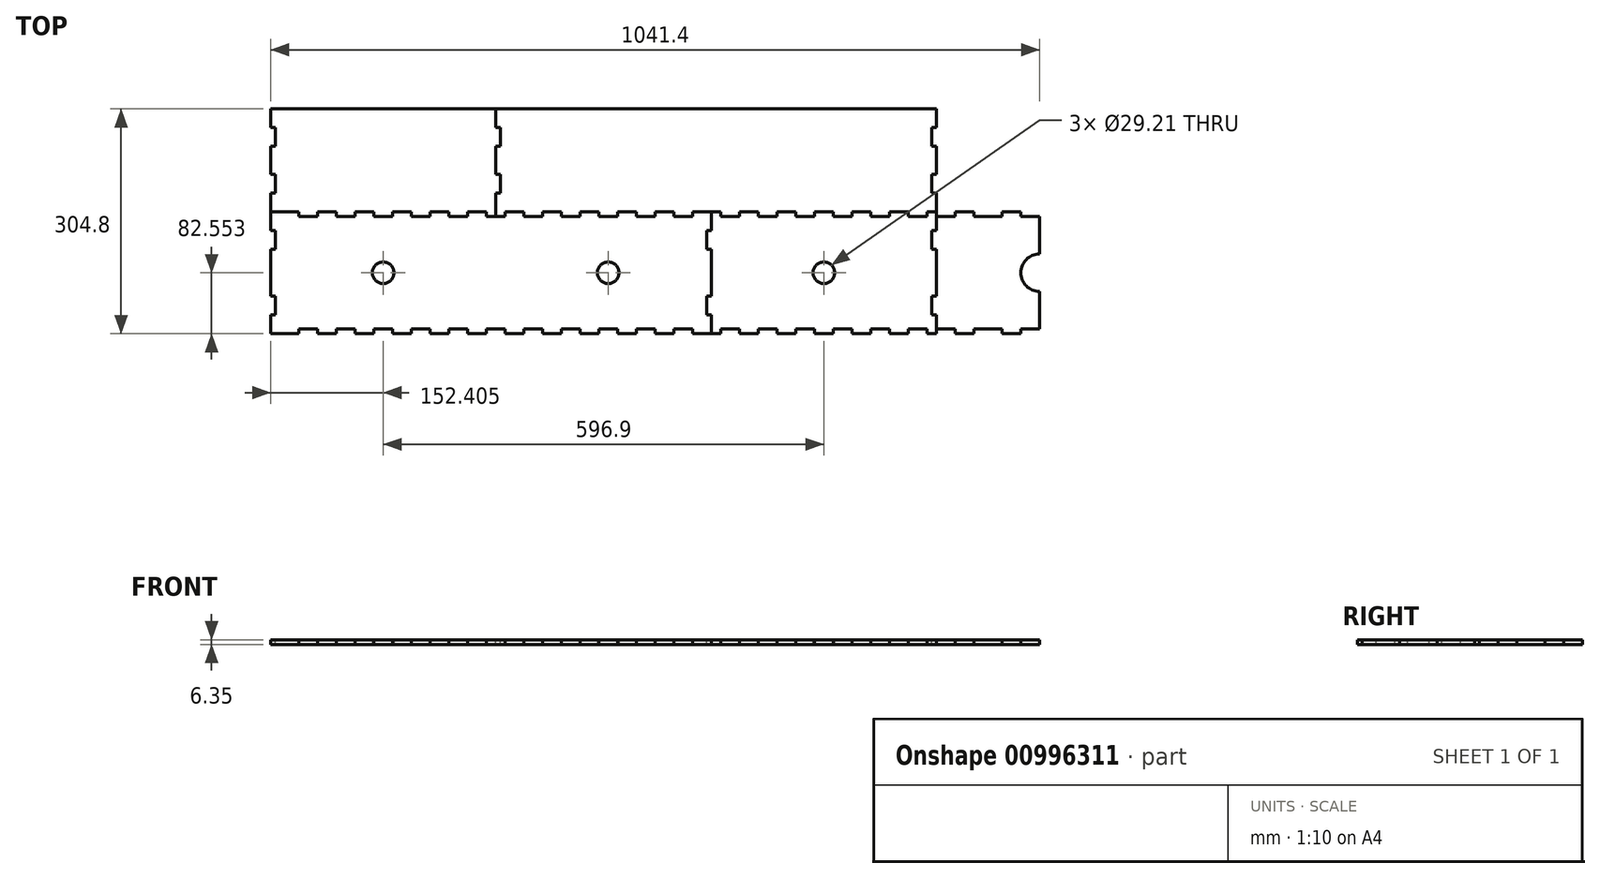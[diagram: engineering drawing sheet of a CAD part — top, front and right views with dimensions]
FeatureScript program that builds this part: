
annotation { "Feature Type Name" : "Feature", "Feature Type Description" : "" }
export const myFeature = defineFeature(function(context is Context, id is Id, definition is map)
    precondition{}
    {
        {
            var Q0;
            Q0=qCreatedBy(makeId("Top.planeOp"),FACE);
            var sketch = newSketch(context, id + "F0", { "sketchPlane" : qUnion([Q0])});
            skLineSegment(sketch, "E0.bottom", {"start": v(-304.97, 96.31) * mm, "end": v(291.93, 96.31) * mm});
            skLineSegment(sketch, "E0.top", {"start": v(-304.97, -68.79) * mm, "end": v(291.93, -68.79) * mm});
            skLineSegment(sketch, "E0.left", {"start": v(-304.97, 96.31) * mm, "end": v(-304.97, -68.79) * mm});
            skLineSegment(sketch, "E0.right", {"start": v(291.93, 96.31) * mm, "end": v(291.93, -68.79) * mm});
            skLineSegment(sketch, "E1.bottom", {"start": v(-266.87, 96.31) * mm, "end": v(-241.47, 96.31) * mm});
            skLineSegment(sketch, "E1.top", {"start": v(-266.87, 89.96) * mm, "end": v(-241.47, 89.96) * mm});
            skLineSegment(sketch, "E1.left", {"start": v(-266.87, 96.31) * mm, "end": v(-266.87, 89.96) * mm});
            skLineSegment(sketch, "E1.right", {"start": v(-241.47, 96.31) * mm, "end": v(-241.47, 89.96) * mm});
            skLineSegment(sketch, "E2.1.0.0", {"start": v(-216.07, 89.96) * mm, "end": v(-190.67, 89.96) * mm});
            skLineSegment(sketch, "E2.1.0.1", {"start": v(-216.07, 96.31) * mm, "end": v(-216.07, 89.96) * mm});
            skLineSegment(sketch, "E2.1.0.2", {"start": v(-216.07, 96.31) * mm, "end": v(-190.67, 96.31) * mm});
            skLineSegment(sketch, "E2.1.0.3", {"start": v(-190.67, 96.31) * mm, "end": v(-190.67, 89.96) * mm});
            skLineSegment(sketch, "E2.2.0.0", {"start": v(-165.27, 89.96) * mm, "end": v(-139.87, 89.96) * mm});
            skLineSegment(sketch, "E2.2.0.1", {"start": v(-165.27, 96.31) * mm, "end": v(-165.27, 89.96) * mm});
            skLineSegment(sketch, "E2.2.0.2", {"start": v(-165.27, 96.31) * mm, "end": v(-139.87, 96.31) * mm});
            skLineSegment(sketch, "E2.2.0.3", {"start": v(-139.87, 96.31) * mm, "end": v(-139.87, 89.96) * mm});
            skLineSegment(sketch, "E2.3.0.0", {"start": v(-114.47, 89.96) * mm, "end": v(-89.07, 89.96) * mm});
            skLineSegment(sketch, "E2.3.0.1", {"start": v(-114.47, 96.31) * mm, "end": v(-114.47, 89.96) * mm});
            skLineSegment(sketch, "E2.3.0.2", {"start": v(-114.47, 96.31) * mm, "end": v(-89.07, 96.31) * mm});
            skLineSegment(sketch, "E2.3.0.3", {"start": v(-89.07, 96.31) * mm, "end": v(-89.07, 89.96) * mm});
            skLineSegment(sketch, "E2.4.0.0", {"start": v(-63.67, 89.96) * mm, "end": v(-38.27, 89.96) * mm});
            skLineSegment(sketch, "E2.4.0.1", {"start": v(-63.67, 96.31) * mm, "end": v(-63.67, 89.96) * mm});
            skLineSegment(sketch, "E2.4.0.2", {"start": v(-63.67, 96.31) * mm, "end": v(-38.27, 96.31) * mm});
            skLineSegment(sketch, "E2.4.0.3", {"start": v(-38.27, 96.31) * mm, "end": v(-38.27, 89.96) * mm});
            skLineSegment(sketch, "E2.5.0.0", {"start": v(-12.87, 89.96) * mm, "end": v(12.53, 89.96) * mm});
            skLineSegment(sketch, "E2.5.0.1", {"start": v(-12.87, 96.31) * mm, "end": v(-12.87, 89.96) * mm});
            skLineSegment(sketch, "E2.5.0.2", {"start": v(-12.87, 96.31) * mm, "end": v(12.53, 96.31) * mm});
            skLineSegment(sketch, "E2.5.0.3", {"start": v(12.53, 96.31) * mm, "end": v(12.53, 89.96) * mm});
            skLineSegment(sketch, "E2.6.0.0", {"start": v(37.93, 89.96) * mm, "end": v(63.33, 89.96) * mm});
            skLineSegment(sketch, "E2.6.0.1", {"start": v(37.93, 96.31) * mm, "end": v(37.93, 89.96) * mm});
            skLineSegment(sketch, "E2.6.0.2", {"start": v(37.93, 96.31) * mm, "end": v(63.33, 96.31) * mm});
            skLineSegment(sketch, "E2.6.0.3", {"start": v(63.33, 96.31) * mm, "end": v(63.33, 89.96) * mm});
            skLineSegment(sketch, "E2.7.0.0", {"start": v(88.73, 89.96) * mm, "end": v(114.13, 89.96) * mm});
            skLineSegment(sketch, "E2.7.0.1", {"start": v(88.73, 96.31) * mm, "end": v(88.73, 89.96) * mm});
            skLineSegment(sketch, "E2.7.0.2", {"start": v(88.73, 96.31) * mm, "end": v(114.13, 96.31) * mm});
            skLineSegment(sketch, "E2.7.0.3", {"start": v(114.13, 96.31) * mm, "end": v(114.13, 89.96) * mm});
            skLineSegment(sketch, "E2.8.0.0", {"start": v(139.53, 89.96) * mm, "end": v(164.93, 89.96) * mm});
            skLineSegment(sketch, "E2.8.0.1", {"start": v(139.53, 96.31) * mm, "end": v(139.53, 89.96) * mm});
            skLineSegment(sketch, "E2.8.0.2", {"start": v(139.53, 96.31) * mm, "end": v(164.93, 96.31) * mm});
            skLineSegment(sketch, "E2.8.0.3", {"start": v(164.93, 96.31) * mm, "end": v(164.93, 89.96) * mm});
            skLineSegment(sketch, "E2.9.0.0", {"start": v(190.33, 89.96) * mm, "end": v(215.73, 89.96) * mm});
            skLineSegment(sketch, "E2.9.0.1", {"start": v(190.33, 96.31) * mm, "end": v(190.33, 89.96) * mm});
            skLineSegment(sketch, "E2.9.0.2", {"start": v(190.33, 96.31) * mm, "end": v(215.73, 96.31) * mm});
            skLineSegment(sketch, "E2.9.0.3", {"start": v(215.73, 96.31) * mm, "end": v(215.73, 89.96) * mm});
            skLineSegment(sketch, "E2.10.0.0", {"start": v(241.13, 89.96) * mm, "end": v(266.53, 89.96) * mm});
            skLineSegment(sketch, "E2.10.0.1", {"start": v(241.13, 96.31) * mm, "end": v(241.13, 89.96) * mm});
            skLineSegment(sketch, "E2.10.0.2", {"start": v(241.13, 96.31) * mm, "end": v(266.53, 96.31) * mm});
            skLineSegment(sketch, "E2.10.0.3", {"start": v(266.53, 96.31) * mm, "end": v(266.53, 89.96) * mm});
            skLineSegment(sketch, "E2.direction1", {"start": v(-266.87, 89.96) * mm, "end": v(-216.07, 89.96) * mm, "construction": true});
            skLineSegment(sketch, "E3.bottom", {"start": v(-266.87, -62.44) * mm, "end": v(-241.47, -62.44) * mm});
            skLineSegment(sketch, "E3.top", {"start": v(-266.87, -68.79) * mm, "end": v(-241.47, -68.79) * mm});
            skLineSegment(sketch, "E3.left", {"start": v(-266.87, -62.44) * mm, "end": v(-266.87, -68.79) * mm});
            skLineSegment(sketch, "E3.right", {"start": v(-241.47, -62.44) * mm, "end": v(-241.47, -68.79) * mm});
            skLineSegment(sketch, "E4.1.0.0", {"start": v(-216.07, -68.79) * mm, "end": v(-190.67, -68.79) * mm});
            skLineSegment(sketch, "E4.1.0.1", {"start": v(-216.07, -62.44) * mm, "end": v(-216.07, -68.79) * mm});
            skLineSegment(sketch, "E4.1.0.2", {"start": v(-216.07, -62.44) * mm, "end": v(-190.67, -62.44) * mm});
            skLineSegment(sketch, "E4.1.0.3", {"start": v(-190.67, -62.44) * mm, "end": v(-190.67, -68.79) * mm});
            skLineSegment(sketch, "E4.2.0.0", {"start": v(-165.27, -68.79) * mm, "end": v(-139.87, -68.79) * mm});
            skLineSegment(sketch, "E4.2.0.1", {"start": v(-165.27, -62.44) * mm, "end": v(-165.27, -68.79) * mm});
            skLineSegment(sketch, "E4.2.0.2", {"start": v(-165.27, -62.44) * mm, "end": v(-139.87, -62.44) * mm});
            skLineSegment(sketch, "E4.2.0.3", {"start": v(-139.87, -62.44) * mm, "end": v(-139.87, -68.79) * mm});
            skLineSegment(sketch, "E4.3.0.0", {"start": v(-114.47, -68.79) * mm, "end": v(-89.07, -68.79) * mm});
            skLineSegment(sketch, "E4.3.0.1", {"start": v(-114.47, -62.44) * mm, "end": v(-114.47, -68.79) * mm});
            skLineSegment(sketch, "E4.3.0.2", {"start": v(-114.47, -62.44) * mm, "end": v(-89.07, -62.44) * mm});
            skLineSegment(sketch, "E4.3.0.3", {"start": v(-89.07, -62.44) * mm, "end": v(-89.07, -68.79) * mm});
            skLineSegment(sketch, "E4.4.0.0", {"start": v(-63.67, -68.79) * mm, "end": v(-38.27, -68.79) * mm});
            skLineSegment(sketch, "E4.4.0.1", {"start": v(-63.67, -62.44) * mm, "end": v(-63.67, -68.79) * mm});
            skLineSegment(sketch, "E4.4.0.2", {"start": v(-63.67, -62.44) * mm, "end": v(-38.27, -62.44) * mm});
            skLineSegment(sketch, "E4.4.0.3", {"start": v(-38.27, -62.44) * mm, "end": v(-38.27, -68.79) * mm});
            skLineSegment(sketch, "E4.5.0.0", {"start": v(-12.87, -68.79) * mm, "end": v(12.53, -68.79) * mm});
            skLineSegment(sketch, "E4.5.0.1", {"start": v(-12.87, -62.44) * mm, "end": v(-12.87, -68.79) * mm});
            skLineSegment(sketch, "E4.5.0.2", {"start": v(-12.87, -62.44) * mm, "end": v(12.53, -62.44) * mm});
            skLineSegment(sketch, "E4.5.0.3", {"start": v(12.53, -62.44) * mm, "end": v(12.53, -68.79) * mm});
            skLineSegment(sketch, "E4.6.0.0", {"start": v(37.93, -68.79) * mm, "end": v(63.33, -68.79) * mm});
            skLineSegment(sketch, "E4.6.0.1", {"start": v(37.93, -62.44) * mm, "end": v(37.93, -68.79) * mm});
            skLineSegment(sketch, "E4.6.0.2", {"start": v(37.93, -62.44) * mm, "end": v(63.33, -62.44) * mm});
            skLineSegment(sketch, "E4.6.0.3", {"start": v(63.33, -62.44) * mm, "end": v(63.33, -68.79) * mm});
            skLineSegment(sketch, "E4.7.0.0", {"start": v(88.73, -68.79) * mm, "end": v(114.13, -68.79) * mm});
            skLineSegment(sketch, "E4.7.0.1", {"start": v(88.73, -62.44) * mm, "end": v(88.73, -68.79) * mm});
            skLineSegment(sketch, "E4.7.0.2", {"start": v(88.73, -62.44) * mm, "end": v(114.13, -62.44) * mm});
            skLineSegment(sketch, "E4.7.0.3", {"start": v(114.13, -62.44) * mm, "end": v(114.13, -68.79) * mm});
            skLineSegment(sketch, "E4.8.0.0", {"start": v(139.53, -68.79) * mm, "end": v(164.93, -68.79) * mm});
            skLineSegment(sketch, "E4.8.0.1", {"start": v(139.53, -62.44) * mm, "end": v(139.53, -68.79) * mm});
            skLineSegment(sketch, "E4.8.0.2", {"start": v(139.53, -62.44) * mm, "end": v(164.93, -62.44) * mm});
            skLineSegment(sketch, "E4.8.0.3", {"start": v(164.93, -62.44) * mm, "end": v(164.93, -68.79) * mm});
            skLineSegment(sketch, "E4.9.0.0", {"start": v(190.33, -68.79) * mm, "end": v(215.73, -68.79) * mm});
            skLineSegment(sketch, "E4.9.0.1", {"start": v(190.33, -62.44) * mm, "end": v(190.33, -68.79) * mm});
            skLineSegment(sketch, "E4.9.0.2", {"start": v(190.33, -62.44) * mm, "end": v(215.73, -62.44) * mm});
            skLineSegment(sketch, "E4.9.0.3", {"start": v(215.73, -62.44) * mm, "end": v(215.73, -68.79) * mm});
            skLineSegment(sketch, "E4.10.0.0", {"start": v(241.13, -68.79) * mm, "end": v(266.53, -68.79) * mm});
            skLineSegment(sketch, "E4.10.0.1", {"start": v(241.13, -62.44) * mm, "end": v(241.13, -68.79) * mm});
            skLineSegment(sketch, "E4.10.0.2", {"start": v(241.13, -62.44) * mm, "end": v(266.53, -62.44) * mm});
            skLineSegment(sketch, "E4.10.0.3", {"start": v(266.53, -62.44) * mm, "end": v(266.53, -68.79) * mm});
            skLineSegment(sketch, "E4.direction1", {"start": v(-266.87, -68.79) * mm, "end": v(-216.07, -68.79) * mm, "construction": true});
            skLineSegment(sketch, "E5.bottom", {"start": v(-304.97, 70.91) * mm, "end": v(-298.62, 70.91) * mm});
            skLineSegment(sketch, "E5.top", {"start": v(-304.97, 45.51) * mm, "end": v(-298.62, 45.51) * mm});
            skLineSegment(sketch, "E5.left", {"start": v(-304.97, 70.91) * mm, "end": v(-304.97, 45.51) * mm});
            skLineSegment(sketch, "E5.right", {"start": v(-298.62, 70.91) * mm, "end": v(-298.62, 45.51) * mm});
            skLineSegment(sketch, "E6.bottom", {"start": v(-304.97, -17.99) * mm, "end": v(-298.62, -17.99) * mm});
            skLineSegment(sketch, "E6.top", {"start": v(-304.97, -43.39) * mm, "end": v(-298.62, -43.39) * mm});
            skLineSegment(sketch, "E6.left", {"start": v(-304.97, -17.99) * mm, "end": v(-304.97, -43.39) * mm});
            skLineSegment(sketch, "E6.right", {"start": v(-298.62, -17.99) * mm, "end": v(-298.62, -43.39) * mm});
            skLineSegment(sketch, "E7.bottom", {"start": v(285.58, 70.91) * mm, "end": v(291.93, 70.91) * mm});
            skLineSegment(sketch, "E7.top", {"start": v(285.58, 45.51) * mm, "end": v(291.93, 45.51) * mm});
            skLineSegment(sketch, "E7.left", {"start": v(285.58, 70.91) * mm, "end": v(285.58, 45.51) * mm});
            skLineSegment(sketch, "E7.right", {"start": v(291.93, 70.91) * mm, "end": v(291.93, 45.51) * mm, "construction": true});
            skLineSegment(sketch, "E8.bottom", {"start": v(285.58, -17.99) * mm, "end": v(291.93, -17.99) * mm});
            skLineSegment(sketch, "E8.top", {"start": v(285.58, -43.39) * mm, "end": v(291.93, -43.39) * mm});
            skLineSegment(sketch, "E8.left", {"start": v(285.58, -17.99) * mm, "end": v(285.58, -43.39) * mm});
            skLineSegment(sketch, "E8.right", {"start": v(291.93, -17.99) * mm, "end": v(291.93, -43.39) * mm});
            skCircle(sketch, "E9", {"center": v(-152.57, 13.76) * mm, "radius": 14.6 * mm});
            skCircle(sketch, "E10", {"center": v(152.23, 13.76) * mm, "radius": 14.6 * mm});
            skSolve(sketch);
        }
        {
            var Q0;
            Q0=makeQuery(id+"F0.imprint","IMPRINT",FACE,{"disambiguationData":[TD([[makeQuery(id+"F0.imprint","IMPRINT",EDGE,{"derivedFrom":sQuery(id+"F0.wireOp",EDGE,"E1.top")}),-1.0]])]});
            extrude(context, id + "F1", {"entities" : qUnion([Q0]), "depth" : 6.35 * mm, "offsetDistance" : 25.4 * mm});
        }
        {
            var Q0;
            Q0=makeQuery(id+"F1.opExtrude","CAP_FACE",FACE,{"disambiguationData":[OSD([sQuery(id+"F0.wireOp",EDGE,"E0.bottom"),sQuery(id+"F0.wireOp",EDGE,"E0.top"),sQuery(id+"F0.wireOp",EDGE,"E0.left"),sQuery(id+"F0.wireOp",EDGE,"E0.right"),sQuery(id+"F0.wireOp",EDGE,"E1.top"),sQuery(id+"F0.wireOp",EDGE,"E1.left"),sQuery(id+"F0.wireOp",EDGE,"E1.right"),sQuery(id+"F0.wireOp",EDGE,"E2.1.0.0"),sQuery(id+"F0.wireOp",EDGE,"E2.1.0.1"),sQuery(id+"F0.wireOp",EDGE,"E2.1.0.3"),sQuery(id+"F0.wireOp",EDGE,"E2.2.0.0"),sQuery(id+"F0.wireOp",EDGE,"E2.2.0.1"),sQuery(id+"F0.wireOp",EDGE,"E2.2.0.3"),sQuery(id+"F0.wireOp",EDGE,"E2.3.0.0"),sQuery(id+"F0.wireOp",EDGE,"E2.3.0.1"),sQuery(id+"F0.wireOp",EDGE,"E2.3.0.3"),sQuery(id+"F0.wireOp",EDGE,"E2.4.0.0"),sQuery(id+"F0.wireOp",EDGE,"E2.4.0.1"),sQuery(id+"F0.wireOp",EDGE,"E2.4.0.3"),sQuery(id+"F0.wireOp",EDGE,"E2.5.0.0"),sQuery(id+"F0.wireOp",EDGE,"E2.5.0.1"),sQuery(id+"F0.wireOp",EDGE,"E2.5.0.3"),sQuery(id+"F0.wireOp",EDGE,"E2.6.0.0"),sQuery(id+"F0.wireOp",EDGE,"E2.6.0.1"),sQuery(id+"F0.wireOp",EDGE,"E2.6.0.3"),sQuery(id+"F0.wireOp",EDGE,"E2.7.0.0"),sQuery(id+"F0.wireOp",EDGE,"E2.7.0.1"),sQuery(id+"F0.wireOp",EDGE,"E2.7.0.3"),sQuery(id+"F0.wireOp",EDGE,"E2.8.0.0"),sQuery(id+"F0.wireOp",EDGE,"E2.8.0.1"),sQuery(id+"F0.wireOp",EDGE,"E2.8.0.3"),sQuery(id+"F0.wireOp",EDGE,"E2.9.0.0"),sQuery(id+"F0.wireOp",EDGE,"E2.9.0.1"),sQuery(id+"F0.wireOp",EDGE,"E2.9.0.3"),sQuery(id+"F0.wireOp",EDGE,"E2.10.0.0"),sQuery(id+"F0.wireOp",EDGE,"E2.10.0.1"),sQuery(id+"F0.wireOp",EDGE,"E2.10.0.3"),sQuery(id+"F0.wireOp",EDGE,"E3.bottom"),sQuery(id+"F0.wireOp",EDGE,"E3.left"),sQuery(id+"F0.wireOp",EDGE,"E3.right"),sQuery(id+"F0.wireOp",EDGE,"E4.1.0.1"),sQuery(id+"F0.wireOp",EDGE,"E4.1.0.2"),sQuery(id+"F0.wireOp",EDGE,"E4.1.0.3"),sQuery(id+"F0.wireOp",EDGE,"E4.2.0.1"),sQuery(id+"F0.wireOp",EDGE,"E4.2.0.2"),sQuery(id+"F0.wireOp",EDGE,"E4.2.0.3"),sQuery(id+"F0.wireOp",EDGE,"E4.3.0.1"),sQuery(id+"F0.wireOp",EDGE,"E4.3.0.2"),sQuery(id+"F0.wireOp",EDGE,"E4.3.0.3"),sQuery(id+"F0.wireOp",EDGE,"E4.4.0.1"),sQuery(id+"F0.wireOp",EDGE,"E4.4.0.2"),sQuery(id+"F0.wireOp",EDGE,"E4.4.0.3"),sQuery(id+"F0.wireOp",EDGE,"E4.5.0.1"),sQuery(id+"F0.wireOp",EDGE,"E4.5.0.2"),sQuery(id+"F0.wireOp",EDGE,"E4.5.0.3"),sQuery(id+"F0.wireOp",EDGE,"E4.6.0.1"),sQuery(id+"F0.wireOp",EDGE,"E4.6.0.2"),sQuery(id+"F0.wireOp",EDGE,"E4.6.0.3"),sQuery(id+"F0.wireOp",EDGE,"E4.7.0.1"),sQuery(id+"F0.wireOp",EDGE,"E4.7.0.2"),sQuery(id+"F0.wireOp",EDGE,"E4.7.0.3"),sQuery(id+"F0.wireOp",EDGE,"E4.8.0.1"),sQuery(id+"F0.wireOp",EDGE,"E4.8.0.2"),sQuery(id+"F0.wireOp",EDGE,"E4.8.0.3"),sQuery(id+"F0.wireOp",EDGE,"E4.9.0.1"),sQuery(id+"F0.wireOp",EDGE,"E4.9.0.2"),sQuery(id+"F0.wireOp",EDGE,"E4.9.0.3"),sQuery(id+"F0.wireOp",EDGE,"E4.10.0.1"),sQuery(id+"F0.wireOp",EDGE,"E4.10.0.2"),sQuery(id+"F0.wireOp",EDGE,"E4.10.0.3"),sQuery(id+"F0.wireOp",EDGE,"E5.bottom"),sQuery(id+"F0.wireOp",EDGE,"E5.top"),sQuery(id+"F0.wireOp",EDGE,"E5.right"),sQuery(id+"F0.wireOp",EDGE,"E6.bottom"),sQuery(id+"F0.wireOp",EDGE,"E6.top"),sQuery(id+"F0.wireOp",EDGE,"E6.right"),sQuery(id+"F0.wireOp",EDGE,"E7.bottom"),sQuery(id+"F0.wireOp",EDGE,"E7.top"),sQuery(id+"F0.wireOp",EDGE,"E7.left"),sQuery(id+"F0.wireOp",EDGE,"E8.bottom"),sQuery(id+"F0.wireOp",EDGE,"E8.top"),sQuery(id+"F0.wireOp",EDGE,"E8.left"),sQuery(id+"F0.wireOp",EDGE,"E9"),sQuery(id+"F0.wireOp",EDGE,"E10")])],"isStart":false});
            var sketch = newSketch(context, id + "F2", { "sketchPlane" : qUnion([Q0])});
            skLineSegment(sketch, "E11.bottom", {"start": v(291.93, 96.31) * mm, "end": v(596.73, 96.31) * mm});
            skLineSegment(sketch, "E11.top", {"start": v(291.93, -68.79) * mm, "end": v(596.73, -68.79) * mm});
            skLineSegment(sketch, "E11.left", {"start": v(291.93, 96.31) * mm, "end": v(291.93, 70.91) * mm});
            skLineSegment(sketch, "E11.right", {"start": v(596.73, 96.31) * mm, "end": v(596.73, -68.79) * mm});
            skLineSegment(sketch, "E12.bottom", {"start": v(291.93, 70.91) * mm, "end": v(285.58, 70.91) * mm});
            skLineSegment(sketch, "E12.top", {"start": v(291.93, 45.51) * mm, "end": v(285.58, 45.51) * mm});
            skLineSegment(sketch, "E12.right", {"start": v(285.58, 70.91) * mm, "end": v(285.58, 45.51) * mm});
            skLineSegment(sketch, "E13.bottom", {"start": v(291.93, -17.99) * mm, "end": v(285.58, -17.99) * mm});
            skLineSegment(sketch, "E13.top", {"start": v(291.93, -43.39) * mm, "end": v(285.58, -43.39) * mm});
            skLineSegment(sketch, "E13.right", {"start": v(285.58, -17.99) * mm, "end": v(285.58, -43.39) * mm});
            skLineSegment(sketch, "E14.trimOffspring", {"start": v(291.93, 45.51) * mm, "end": v(291.93, -17.99) * mm});
            skLineSegment(sketch, "E15.trimOffspring", {"start": v(291.93, -43.39) * mm, "end": v(291.93, -68.79) * mm});
            skLineSegment(sketch, "E16.bottom", {"start": v(304.63, 96.31) * mm, "end": v(330.03, 96.31) * mm});
            skLineSegment(sketch, "E16.top", {"start": v(304.63, 89.96) * mm, "end": v(330.03, 89.96) * mm});
            skLineSegment(sketch, "E16.left", {"start": v(304.63, 96.31) * mm, "end": v(304.63, 89.96) * mm});
            skLineSegment(sketch, "E16.right", {"start": v(330.03, 96.31) * mm, "end": v(330.03, 89.96) * mm});
            skLineSegment(sketch, "E17.1.0.0", {"start": v(355.43, 96.31) * mm, "end": v(380.83, 96.31) * mm});
            skLineSegment(sketch, "E17.1.0.1", {"start": v(355.43, 89.96) * mm, "end": v(380.83, 89.96) * mm});
            skLineSegment(sketch, "E17.1.0.2", {"start": v(355.43, 96.31) * mm, "end": v(355.43, 89.96) * mm});
            skLineSegment(sketch, "E17.1.0.3", {"start": v(380.83, 96.31) * mm, "end": v(380.83, 89.96) * mm});
            skLineSegment(sketch, "E17.2.0.0", {"start": v(406.23, 96.31) * mm, "end": v(431.63, 96.31) * mm});
            skLineSegment(sketch, "E17.2.0.1", {"start": v(406.23, 89.96) * mm, "end": v(431.63, 89.96) * mm});
            skLineSegment(sketch, "E17.2.0.2", {"start": v(406.23, 96.31) * mm, "end": v(406.23, 89.96) * mm});
            skLineSegment(sketch, "E17.2.0.3", {"start": v(431.63, 96.31) * mm, "end": v(431.63, 89.96) * mm});
            skLineSegment(sketch, "E17.3.0.0", {"start": v(457.03, 96.31) * mm, "end": v(482.43, 96.31) * mm});
            skLineSegment(sketch, "E17.3.0.1", {"start": v(457.03, 89.96) * mm, "end": v(482.43, 89.96) * mm});
            skLineSegment(sketch, "E17.3.0.2", {"start": v(457.03, 96.31) * mm, "end": v(457.03, 89.96) * mm});
            skLineSegment(sketch, "E17.3.0.3", {"start": v(482.43, 96.31) * mm, "end": v(482.43, 89.96) * mm});
            skLineSegment(sketch, "E17.4.0.0", {"start": v(507.83, 96.31) * mm, "end": v(533.23, 96.31) * mm});
            skLineSegment(sketch, "E17.4.0.1", {"start": v(507.83, 89.96) * mm, "end": v(533.23, 89.96) * mm});
            skLineSegment(sketch, "E17.4.0.2", {"start": v(507.83, 96.31) * mm, "end": v(507.83, 89.96) * mm});
            skLineSegment(sketch, "E17.4.0.3", {"start": v(533.23, 96.31) * mm, "end": v(533.23, 89.96) * mm});
            skLineSegment(sketch, "E17.5.0.0", {"start": v(558.63, 96.31) * mm, "end": v(584.03, 96.31) * mm});
            skLineSegment(sketch, "E17.5.0.1", {"start": v(558.63, 89.96) * mm, "end": v(584.03, 89.96) * mm});
            skLineSegment(sketch, "E17.5.0.2", {"start": v(558.63, 96.31) * mm, "end": v(558.63, 89.96) * mm});
            skLineSegment(sketch, "E17.5.0.3", {"start": v(584.03, 96.31) * mm, "end": v(584.03, 89.96) * mm});
            skLineSegment(sketch, "E17.direction1", {"start": v(304.63, 89.96) * mm, "end": v(355.43, 89.96) * mm, "construction": true});
            skLineSegment(sketch, "E18.bottom", {"start": v(304.63, -68.79) * mm, "end": v(330.03, -68.79) * mm});
            skLineSegment(sketch, "E18.top", {"start": v(304.63, -62.44) * mm, "end": v(330.03, -62.44) * mm});
            skLineSegment(sketch, "E18.left", {"start": v(304.63, -68.79) * mm, "end": v(304.63, -62.44) * mm});
            skLineSegment(sketch, "E18.right", {"start": v(330.03, -68.79) * mm, "end": v(330.03, -62.44) * mm});
            skLineSegment(sketch, "E19.1.0.0", {"start": v(355.43, -68.79) * mm, "end": v(355.43, -62.44) * mm});
            skLineSegment(sketch, "E19.1.0.1", {"start": v(355.43, -68.79) * mm, "end": v(380.83, -68.79) * mm});
            skLineSegment(sketch, "E19.1.0.2", {"start": v(380.83, -68.79) * mm, "end": v(380.83, -62.44) * mm});
            skLineSegment(sketch, "E19.1.0.3", {"start": v(355.43, -62.44) * mm, "end": v(380.83, -62.44) * mm});
            skLineSegment(sketch, "E19.2.0.0", {"start": v(406.23, -68.79) * mm, "end": v(406.23, -62.44) * mm});
            skLineSegment(sketch, "E19.2.0.1", {"start": v(406.23, -68.79) * mm, "end": v(431.63, -68.79) * mm});
            skLineSegment(sketch, "E19.2.0.2", {"start": v(431.63, -68.79) * mm, "end": v(431.63, -62.44) * mm});
            skLineSegment(sketch, "E19.2.0.3", {"start": v(406.23, -62.44) * mm, "end": v(431.63, -62.44) * mm});
            skLineSegment(sketch, "E19.3.0.0", {"start": v(457.03, -68.79) * mm, "end": v(457.03, -62.44) * mm});
            skLineSegment(sketch, "E19.3.0.1", {"start": v(457.03, -68.79) * mm, "end": v(482.43, -68.79) * mm});
            skLineSegment(sketch, "E19.3.0.2", {"start": v(482.43, -68.79) * mm, "end": v(482.43, -62.44) * mm});
            skLineSegment(sketch, "E19.3.0.3", {"start": v(457.03, -62.44) * mm, "end": v(482.43, -62.44) * mm});
            skLineSegment(sketch, "E19.4.0.0", {"start": v(507.83, -68.79) * mm, "end": v(507.83, -62.44) * mm});
            skLineSegment(sketch, "E19.4.0.1", {"start": v(507.83, -68.79) * mm, "end": v(533.23, -68.79) * mm});
            skLineSegment(sketch, "E19.4.0.2", {"start": v(533.23, -68.79) * mm, "end": v(533.23, -62.44) * mm});
            skLineSegment(sketch, "E19.4.0.3", {"start": v(507.83, -62.44) * mm, "end": v(533.23, -62.44) * mm});
            skLineSegment(sketch, "E19.5.0.0", {"start": v(558.63, -68.79) * mm, "end": v(558.63, -62.44) * mm});
            skLineSegment(sketch, "E19.5.0.1", {"start": v(558.63, -68.79) * mm, "end": v(584.03, -68.79) * mm});
            skLineSegment(sketch, "E19.5.0.2", {"start": v(584.03, -68.79) * mm, "end": v(584.03, -62.44) * mm});
            skLineSegment(sketch, "E19.5.0.3", {"start": v(558.63, -62.44) * mm, "end": v(584.03, -62.44) * mm});
            skLineSegment(sketch, "E19.direction1", {"start": v(304.63, -68.79) * mm, "end": v(355.43, -68.79) * mm, "construction": true});
            skLineSegment(sketch, "E20.bottom", {"start": v(596.73, 70.91) * mm, "end": v(590.38, 70.91) * mm});
            skLineSegment(sketch, "E20.top", {"start": v(596.73, 45.51) * mm, "end": v(590.38, 45.51) * mm});
            skLineSegment(sketch, "E20.left", {"start": v(596.73, 70.91) * mm, "end": v(596.73, 45.51) * mm});
            skLineSegment(sketch, "E20.right", {"start": v(590.38, 70.91) * mm, "end": v(590.38, 45.51) * mm});
            skLineSegment(sketch, "E21.bottom", {"start": v(596.73, -43.39) * mm, "end": v(590.38, -43.39) * mm});
            skLineSegment(sketch, "E21.top", {"start": v(596.73, -17.99) * mm, "end": v(590.38, -17.99) * mm});
            skLineSegment(sketch, "E21.left", {"start": v(596.73, -43.39) * mm, "end": v(596.73, -17.99) * mm});
            skLineSegment(sketch, "E21.right", {"start": v(590.38, -43.39) * mm, "end": v(590.38, -17.99) * mm});
            skCircle(sketch, "E22", {"center": v(444.33, 13.76) * mm, "radius": 14.6 * mm});
            skSolve(sketch);
        }
        {
            var Q0;
            {var subQ30=sQuery(id+"F2.wireOp",EDGE,"E11.left");Q0=makeQuery(id+"F2.imprint","IMPRINT",FACE,{"disambiguationData":[TD([[makeQuery(id+"F2.imprint","IMPRINT",EDGE,{"derivedFrom":subQ30}),1.0]])]});}
            extrude(context, id + "F3", {"entities" : qUnion([Q0]), "oppositeDirection" : true, "depth" : 6.35 * mm, "offsetDistance" : 25.4 * mm});
        }
        {
            var Q0;
            Q0=makeQuery(id+"F3.opExtrude","CAP_FACE",FACE,{"disambiguationData":[OSD([sQuery(id+"F2.wireOp",EDGE,"E11.bottom"),sQuery(id+"F2.wireOp",EDGE,"E11.top"),sQuery(id+"F2.wireOp",EDGE,"E11.left"),sQuery(id+"F2.wireOp",EDGE,"E11.right"),sQuery(id+"F2.wireOp",EDGE,"E12.bottom"),sQuery(id+"F2.wireOp",EDGE,"E12.top"),sQuery(id+"F2.wireOp",EDGE,"E12.right"),sQuery(id+"F2.wireOp",EDGE,"E13.bottom"),sQuery(id+"F2.wireOp",EDGE,"E13.top"),sQuery(id+"F2.wireOp",EDGE,"E13.right"),sQuery(id+"F2.wireOp",EDGE,"E14.trimOffspring"),sQuery(id+"F2.wireOp",EDGE,"E15.trimOffspring"),sQuery(id+"F2.wireOp",EDGE,"E16.top"),sQuery(id+"F2.wireOp",EDGE,"E16.left"),sQuery(id+"F2.wireOp",EDGE,"E16.right"),sQuery(id+"F2.wireOp",EDGE,"E17.1.0.1"),sQuery(id+"F2.wireOp",EDGE,"E17.1.0.2"),sQuery(id+"F2.wireOp",EDGE,"E17.1.0.3"),sQuery(id+"F2.wireOp",EDGE,"E17.2.0.1"),sQuery(id+"F2.wireOp",EDGE,"E17.2.0.2"),sQuery(id+"F2.wireOp",EDGE,"E17.2.0.3"),sQuery(id+"F2.wireOp",EDGE,"E17.3.0.1"),sQuery(id+"F2.wireOp",EDGE,"E17.3.0.2"),sQuery(id+"F2.wireOp",EDGE,"E17.3.0.3"),sQuery(id+"F2.wireOp",EDGE,"E17.4.0.1"),sQuery(id+"F2.wireOp",EDGE,"E17.4.0.2"),sQuery(id+"F2.wireOp",EDGE,"E17.4.0.3"),sQuery(id+"F2.wireOp",EDGE,"E17.5.0.1"),sQuery(id+"F2.wireOp",EDGE,"E17.5.0.2"),sQuery(id+"F2.wireOp",EDGE,"E17.5.0.3"),sQuery(id+"F2.wireOp",EDGE,"E18.top"),sQuery(id+"F2.wireOp",EDGE,"E18.left"),sQuery(id+"F2.wireOp",EDGE,"E18.right"),sQuery(id+"F2.wireOp",EDGE,"E19.1.0.0"),sQuery(id+"F2.wireOp",EDGE,"E19.1.0.2"),sQuery(id+"F2.wireOp",EDGE,"E19.1.0.3"),sQuery(id+"F2.wireOp",EDGE,"E19.2.0.0"),sQuery(id+"F2.wireOp",EDGE,"E19.2.0.2"),sQuery(id+"F2.wireOp",EDGE,"E19.2.0.3"),sQuery(id+"F2.wireOp",EDGE,"E19.3.0.0"),sQuery(id+"F2.wireOp",EDGE,"E19.3.0.2"),sQuery(id+"F2.wireOp",EDGE,"E19.3.0.3"),sQuery(id+"F2.wireOp",EDGE,"E19.4.0.0"),sQuery(id+"F2.wireOp",EDGE,"E19.4.0.2"),sQuery(id+"F2.wireOp",EDGE,"E19.4.0.3"),sQuery(id+"F2.wireOp",EDGE,"E19.5.0.0"),sQuery(id+"F2.wireOp",EDGE,"E19.5.0.2"),sQuery(id+"F2.wireOp",EDGE,"E19.5.0.3"),sQuery(id+"F2.wireOp",EDGE,"E20.bottom"),sQuery(id+"F2.wireOp",EDGE,"E20.top"),sQuery(id+"F2.wireOp",EDGE,"E20.right"),sQuery(id+"F2.wireOp",EDGE,"E21.bottom"),sQuery(id+"F2.wireOp",EDGE,"E21.top"),sQuery(id+"F2.wireOp",EDGE,"E21.right"),sQuery(id+"F2.wireOp",EDGE,"E22")])],"isStart":true});
            var sketch = newSketch(context, id + "F4", { "sketchPlane" : qUnion([Q0])});
            skLineSegment(sketch, "E23.bottom", {"start": v(596.73, 96.31) * mm, "end": v(-0.17, 96.31) * mm});
            skLineSegment(sketch, "E23.top", {"start": v(596.73, 236.01) * mm, "end": v(-0.17, 236.01) * mm});
            skLineSegment(sketch, "E23.left", {"start": v(596.73, 96.31) * mm, "end": v(596.73, 121.71) * mm});
            skLineSegment(sketch, "E23.right", {"start": v(-0.17, 96.31) * mm, "end": v(-0.17, 121.71) * mm});
            skLineSegment(sketch, "E24.bottom", {"start": v(-0.17, 96.31) * mm, "end": v(12.53, 96.31) * mm});
            skLineSegment(sketch, "E24.top", {"start": v(-0.17, 89.96) * mm, "end": v(12.53, 89.96) * mm});
            skLineSegment(sketch, "E24.left", {"start": v(-0.17, 96.31) * mm, "end": v(-0.17, 89.96) * mm});
            skLineSegment(sketch, "E24.right", {"start": v(12.53, 96.31) * mm, "end": v(12.53, 89.96) * mm});
            skLineSegment(sketch, "E25.bottom", {"start": v(584.03, 96.31) * mm, "end": v(558.63, 96.31) * mm});
            skLineSegment(sketch, "E25.top", {"start": v(584.03, 89.96) * mm, "end": v(558.63, 89.96) * mm});
            skLineSegment(sketch, "E25.left", {"start": v(584.03, 96.31) * mm, "end": v(584.03, 89.96) * mm});
            skLineSegment(sketch, "E25.right", {"start": v(558.63, 96.31) * mm, "end": v(558.63, 89.96) * mm});
            skLineSegment(sketch, "E26.bottom", {"start": v(533.23, 96.31) * mm, "end": v(507.83, 96.31) * mm});
            skLineSegment(sketch, "E26.top", {"start": v(533.23, 89.96) * mm, "end": v(507.83, 89.96) * mm});
            skLineSegment(sketch, "E26.left", {"start": v(533.23, 96.31) * mm, "end": v(533.23, 89.96) * mm});
            skLineSegment(sketch, "E26.right", {"start": v(507.83, 96.31) * mm, "end": v(507.83, 89.96) * mm});
            skLineSegment(sketch, "E27.bottom", {"start": v(482.43, 96.31) * mm, "end": v(457.03, 96.31) * mm});
            skLineSegment(sketch, "E27.top", {"start": v(482.43, 89.96) * mm, "end": v(457.03, 89.96) * mm});
            skLineSegment(sketch, "E27.left", {"start": v(482.43, 96.31) * mm, "end": v(482.43, 89.96) * mm});
            skLineSegment(sketch, "E27.right", {"start": v(457.03, 96.31) * mm, "end": v(457.03, 89.96) * mm});
            skLineSegment(sketch, "E28.bottom", {"start": v(431.63, 96.31) * mm, "end": v(406.23, 96.31) * mm});
            skLineSegment(sketch, "E28.top", {"start": v(431.63, 89.96) * mm, "end": v(406.23, 89.96) * mm});
            skLineSegment(sketch, "E28.left", {"start": v(431.63, 96.31) * mm, "end": v(431.63, 89.96) * mm});
            skLineSegment(sketch, "E28.right", {"start": v(406.23, 96.31) * mm, "end": v(406.23, 89.96) * mm});
            skLineSegment(sketch, "E29.bottom", {"start": v(380.83, 96.31) * mm, "end": v(355.43, 96.31) * mm});
            skLineSegment(sketch, "E29.top", {"start": v(380.83, 89.96) * mm, "end": v(355.43, 89.96) * mm});
            skLineSegment(sketch, "E29.left", {"start": v(380.83, 96.31) * mm, "end": v(380.83, 89.96) * mm});
            skLineSegment(sketch, "E29.right", {"start": v(355.43, 96.31) * mm, "end": v(355.43, 89.96) * mm});
            skLineSegment(sketch, "E30.bottom", {"start": v(330.03, 96.31) * mm, "end": v(304.63, 96.31) * mm});
            skLineSegment(sketch, "E30.top", {"start": v(330.03, 89.96) * mm, "end": v(304.63, 89.96) * mm});
            skLineSegment(sketch, "E30.left", {"start": v(330.03, 96.31) * mm, "end": v(330.03, 89.96) * mm});
            skLineSegment(sketch, "E30.right", {"start": v(304.63, 96.31) * mm, "end": v(304.63, 89.96) * mm});
            skLineSegment(sketch, "E31.bottom", {"start": v(266.53, 96.31) * mm, "end": v(241.13, 96.31) * mm});
            skLineSegment(sketch, "E31.top", {"start": v(266.53, 89.96) * mm, "end": v(241.13, 89.96) * mm});
            skLineSegment(sketch, "E31.left", {"start": v(266.53, 96.31) * mm, "end": v(266.53, 89.96) * mm});
            skLineSegment(sketch, "E31.right", {"start": v(241.13, 96.31) * mm, "end": v(241.13, 89.96) * mm});
            skLineSegment(sketch, "E32.1.0.0", {"start": v(215.73, 96.31) * mm, "end": v(190.33, 96.31) * mm});
            skLineSegment(sketch, "E32.1.0.1", {"start": v(190.33, 96.31) * mm, "end": v(190.33, 89.96) * mm});
            skLineSegment(sketch, "E32.1.0.2", {"start": v(215.73, 89.96) * mm, "end": v(190.33, 89.96) * mm});
            skLineSegment(sketch, "E32.1.0.3", {"start": v(215.73, 96.31) * mm, "end": v(215.73, 89.96) * mm});
            skLineSegment(sketch, "E32.2.0.0", {"start": v(164.93, 96.31) * mm, "end": v(139.53, 96.31) * mm});
            skLineSegment(sketch, "E32.2.0.1", {"start": v(139.53, 96.31) * mm, "end": v(139.53, 89.96) * mm});
            skLineSegment(sketch, "E32.2.0.2", {"start": v(164.93, 89.96) * mm, "end": v(139.53, 89.96) * mm});
            skLineSegment(sketch, "E32.2.0.3", {"start": v(164.93, 96.31) * mm, "end": v(164.93, 89.96) * mm});
            skLineSegment(sketch, "E32.3.0.0", {"start": v(114.13, 96.31) * mm, "end": v(88.73, 96.31) * mm});
            skLineSegment(sketch, "E32.3.0.1", {"start": v(88.73, 96.31) * mm, "end": v(88.73, 89.96) * mm});
            skLineSegment(sketch, "E32.3.0.2", {"start": v(114.13, 89.96) * mm, "end": v(88.73, 89.96) * mm});
            skLineSegment(sketch, "E32.3.0.3", {"start": v(114.13, 96.31) * mm, "end": v(114.13, 89.96) * mm});
            skLineSegment(sketch, "E32.4.0.0", {"start": v(63.33, 96.31) * mm, "end": v(37.93, 96.31) * mm});
            skLineSegment(sketch, "E32.4.0.1", {"start": v(37.93, 96.31) * mm, "end": v(37.93, 89.96) * mm});
            skLineSegment(sketch, "E32.4.0.2", {"start": v(63.33, 89.96) * mm, "end": v(37.93, 89.96) * mm});
            skLineSegment(sketch, "E32.4.0.3", {"start": v(63.33, 96.31) * mm, "end": v(63.33, 89.96) * mm});
            skLineSegment(sketch, "E32.direction1", {"start": v(241.13, 89.96) * mm, "end": v(190.33, 89.96) * mm, "construction": true});
            skLineSegment(sketch, "E33.bottom", {"start": v(596.73, 210.61) * mm, "end": v(590.38, 210.61) * mm});
            skLineSegment(sketch, "E33.top", {"start": v(596.73, 185.21) * mm, "end": v(590.38, 185.21) * mm});
            skLineSegment(sketch, "E33.right", {"start": v(590.38, 210.61) * mm, "end": v(590.38, 185.21) * mm});
            skLineSegment(sketch, "E34.bottom", {"start": v(596.73, 121.71) * mm, "end": v(590.38, 121.71) * mm});
            skLineSegment(sketch, "E34.top", {"start": v(596.73, 147.11) * mm, "end": v(590.38, 147.11) * mm});
            skLineSegment(sketch, "E34.right", {"start": v(590.38, 121.71) * mm, "end": v(590.38, 147.11) * mm});
            skLineSegment(sketch, "E35.bottom", {"start": v(-0.17, 210.61) * mm, "end": v(6.18, 210.61) * mm});
            skLineSegment(sketch, "E35.top", {"start": v(-0.17, 185.21) * mm, "end": v(6.18, 185.21) * mm});
            skLineSegment(sketch, "E35.right", {"start": v(6.18, 210.61) * mm, "end": v(6.18, 185.21) * mm});
            skLineSegment(sketch, "E36.bottom", {"start": v(-0.17, 147.11) * mm, "end": v(6.18, 147.11) * mm});
            skLineSegment(sketch, "E36.top", {"start": v(-0.17, 121.71) * mm, "end": v(6.18, 121.71) * mm});
            skLineSegment(sketch, "E36.right", {"start": v(6.18, 147.11) * mm, "end": v(6.18, 121.71) * mm});
            skLineSegment(sketch, "E37.trimOffspring", {"start": v(-0.17, 210.61) * mm, "end": v(-0.17, 236.01) * mm});
            skLineSegment(sketch, "E38.trimOffspring", {"start": v(-0.17, 147.11) * mm, "end": v(-0.17, 185.21) * mm});
            skLineSegment(sketch, "E39.trimOffspring", {"start": v(596.73, 210.61) * mm, "end": v(596.73, 236.01) * mm});
            skLineSegment(sketch, "E40.trimOffspring", {"start": v(596.73, 147.11) * mm, "end": v(596.73, 185.21) * mm});
            skSolve(sketch);
        }
        {
            var Q0;
            Q0 = qSketchRegion(id + "F4", true);
            extrude(context, id + "F5", {"entities" : qUnion([Q0]), "oppositeDirection" : true, "depth" : 6.35 * mm, "offsetDistance" : 25.4 * mm});
        }
        {
            var Q0;
            Q0=makeQuery(id+"F1.opExtrude","CAP_FACE",FACE,{"disambiguationData":[OSD([sQuery(id+"F0.wireOp",EDGE,"E0.bottom"),sQuery(id+"F0.wireOp",EDGE,"E0.top"),sQuery(id+"F0.wireOp",EDGE,"E0.left"),sQuery(id+"F0.wireOp",EDGE,"E0.right"),sQuery(id+"F0.wireOp",EDGE,"E1.top"),sQuery(id+"F0.wireOp",EDGE,"E1.left"),sQuery(id+"F0.wireOp",EDGE,"E1.right"),sQuery(id+"F0.wireOp",EDGE,"E2.1.0.0"),sQuery(id+"F0.wireOp",EDGE,"E2.1.0.1"),sQuery(id+"F0.wireOp",EDGE,"E2.1.0.3"),sQuery(id+"F0.wireOp",EDGE,"E2.2.0.0"),sQuery(id+"F0.wireOp",EDGE,"E2.2.0.1"),sQuery(id+"F0.wireOp",EDGE,"E2.2.0.3"),sQuery(id+"F0.wireOp",EDGE,"E2.3.0.0"),sQuery(id+"F0.wireOp",EDGE,"E2.3.0.1"),sQuery(id+"F0.wireOp",EDGE,"E2.3.0.3"),sQuery(id+"F0.wireOp",EDGE,"E2.4.0.0"),sQuery(id+"F0.wireOp",EDGE,"E2.4.0.1"),sQuery(id+"F0.wireOp",EDGE,"E2.4.0.3"),sQuery(id+"F0.wireOp",EDGE,"E2.5.0.0"),sQuery(id+"F0.wireOp",EDGE,"E2.5.0.1"),sQuery(id+"F0.wireOp",EDGE,"E2.5.0.3"),sQuery(id+"F0.wireOp",EDGE,"E2.6.0.0"),sQuery(id+"F0.wireOp",EDGE,"E2.6.0.1"),sQuery(id+"F0.wireOp",EDGE,"E2.6.0.3"),sQuery(id+"F0.wireOp",EDGE,"E2.7.0.0"),sQuery(id+"F0.wireOp",EDGE,"E2.7.0.1"),sQuery(id+"F0.wireOp",EDGE,"E2.7.0.3"),sQuery(id+"F0.wireOp",EDGE,"E2.8.0.0"),sQuery(id+"F0.wireOp",EDGE,"E2.8.0.1"),sQuery(id+"F0.wireOp",EDGE,"E2.8.0.3"),sQuery(id+"F0.wireOp",EDGE,"E2.9.0.0"),sQuery(id+"F0.wireOp",EDGE,"E2.9.0.1"),sQuery(id+"F0.wireOp",EDGE,"E2.9.0.3"),sQuery(id+"F0.wireOp",EDGE,"E2.10.0.0"),sQuery(id+"F0.wireOp",EDGE,"E2.10.0.1"),sQuery(id+"F0.wireOp",EDGE,"E2.10.0.3"),sQuery(id+"F0.wireOp",EDGE,"E3.bottom"),sQuery(id+"F0.wireOp",EDGE,"E3.left"),sQuery(id+"F0.wireOp",EDGE,"E3.right"),sQuery(id+"F0.wireOp",EDGE,"E4.1.0.1"),sQuery(id+"F0.wireOp",EDGE,"E4.1.0.2"),sQuery(id+"F0.wireOp",EDGE,"E4.1.0.3"),sQuery(id+"F0.wireOp",EDGE,"E4.2.0.1"),sQuery(id+"F0.wireOp",EDGE,"E4.2.0.2"),sQuery(id+"F0.wireOp",EDGE,"E4.2.0.3"),sQuery(id+"F0.wireOp",EDGE,"E4.3.0.1"),sQuery(id+"F0.wireOp",EDGE,"E4.3.0.2"),sQuery(id+"F0.wireOp",EDGE,"E4.3.0.3"),sQuery(id+"F0.wireOp",EDGE,"E4.4.0.1"),sQuery(id+"F0.wireOp",EDGE,"E4.4.0.2"),sQuery(id+"F0.wireOp",EDGE,"E4.4.0.3"),sQuery(id+"F0.wireOp",EDGE,"E4.5.0.1"),sQuery(id+"F0.wireOp",EDGE,"E4.5.0.2"),sQuery(id+"F0.wireOp",EDGE,"E4.5.0.3"),sQuery(id+"F0.wireOp",EDGE,"E4.6.0.1"),sQuery(id+"F0.wireOp",EDGE,"E4.6.0.2"),sQuery(id+"F0.wireOp",EDGE,"E4.6.0.3"),sQuery(id+"F0.wireOp",EDGE,"E4.7.0.1"),sQuery(id+"F0.wireOp",EDGE,"E4.7.0.2"),sQuery(id+"F0.wireOp",EDGE,"E4.7.0.3"),sQuery(id+"F0.wireOp",EDGE,"E4.8.0.1"),sQuery(id+"F0.wireOp",EDGE,"E4.8.0.2"),sQuery(id+"F0.wireOp",EDGE,"E4.8.0.3"),sQuery(id+"F0.wireOp",EDGE,"E4.9.0.1"),sQuery(id+"F0.wireOp",EDGE,"E4.9.0.2"),sQuery(id+"F0.wireOp",EDGE,"E4.9.0.3"),sQuery(id+"F0.wireOp",EDGE,"E4.10.0.1"),sQuery(id+"F0.wireOp",EDGE,"E4.10.0.2"),sQuery(id+"F0.wireOp",EDGE,"E4.10.0.3"),sQuery(id+"F0.wireOp",EDGE,"E5.bottom"),sQuery(id+"F0.wireOp",EDGE,"E5.top"),sQuery(id+"F0.wireOp",EDGE,"E5.right"),sQuery(id+"F0.wireOp",EDGE,"E6.bottom"),sQuery(id+"F0.wireOp",EDGE,"E6.top"),sQuery(id+"F0.wireOp",EDGE,"E6.right"),sQuery(id+"F0.wireOp",EDGE,"E7.bottom"),sQuery(id+"F0.wireOp",EDGE,"E7.top"),sQuery(id+"F0.wireOp",EDGE,"E7.left"),sQuery(id+"F0.wireOp",EDGE,"E8.bottom"),sQuery(id+"F0.wireOp",EDGE,"E8.top"),sQuery(id+"F0.wireOp",EDGE,"E8.left"),sQuery(id+"F0.wireOp",EDGE,"E9"),sQuery(id+"F0.wireOp",EDGE,"E10")])],"isStart":false});
            var sketch = newSketch(context, id + "F6", { "sketchPlane" : qUnion([Q0])});
            skPoint(sketch, "E41.oppositeSnap0", {"position": v(-0.17, 89.96) * mm});
            skLineSegment(sketch, "E41.bottom", {"start": v(-304.97, 236.01) * mm, "end": v(-0.17, 236.01) * mm});
            skLineSegment(sketch, "E41.top", {"start": v(-304.97, 96.31) * mm, "end": v(-0.17, 96.31) * mm});
            skLineSegment(sketch, "E41.left", {"start": v(-304.97, 236.01) * mm, "end": v(-304.97, 210.61) * mm});
            skLineSegment(sketch, "E41.right", {"start": v(-0.17, 236.01) * mm, "end": v(-0.17, 96.31) * mm});
            skLineSegment(sketch, "E42.bottom", {"start": v(-266.87, 96.31) * mm, "end": v(-241.47, 96.31) * mm});
            skLineSegment(sketch, "E42.top", {"start": v(-266.87, 89.96) * mm, "end": v(-241.47, 89.96) * mm});
            skLineSegment(sketch, "E42.left", {"start": v(-266.87, 96.31) * mm, "end": v(-266.87, 89.96) * mm});
            skLineSegment(sketch, "E42.right", {"start": v(-241.47, 96.31) * mm, "end": v(-241.47, 89.96) * mm});
            skLineSegment(sketch, "E43.bottom", {"start": v(-216.07, 96.31) * mm, "end": v(-190.67, 96.31) * mm});
            skLineSegment(sketch, "E43.top", {"start": v(-216.07, 89.96) * mm, "end": v(-190.67, 89.96) * mm});
            skLineSegment(sketch, "E43.left", {"start": v(-216.07, 96.31) * mm, "end": v(-216.07, 89.96) * mm});
            skLineSegment(sketch, "E43.right", {"start": v(-190.67, 96.31) * mm, "end": v(-190.67, 89.96) * mm});
            skLineSegment(sketch, "E44.bottom", {"start": v(-165.27, 96.31) * mm, "end": v(-139.87, 96.31) * mm});
            skLineSegment(sketch, "E44.top", {"start": v(-165.27, 89.96) * mm, "end": v(-139.87, 89.96) * mm});
            skLineSegment(sketch, "E44.left", {"start": v(-165.27, 96.31) * mm, "end": v(-165.27, 89.96) * mm});
            skLineSegment(sketch, "E44.right", {"start": v(-139.87, 96.31) * mm, "end": v(-139.87, 89.96) * mm});
            skLineSegment(sketch, "E45.bottom", {"start": v(-114.47, 96.31) * mm, "end": v(-89.07, 96.31) * mm});
            skLineSegment(sketch, "E45.top", {"start": v(-114.47, 89.96) * mm, "end": v(-89.07, 89.96) * mm});
            skLineSegment(sketch, "E45.left", {"start": v(-114.47, 96.31) * mm, "end": v(-114.47, 89.96) * mm});
            skLineSegment(sketch, "E45.right", {"start": v(-89.07, 96.31) * mm, "end": v(-89.07, 89.96) * mm});
            skLineSegment(sketch, "E46.bottom", {"start": v(-63.67, 96.31) * mm, "end": v(-38.27, 96.31) * mm});
            skLineSegment(sketch, "E46.top", {"start": v(-63.67, 89.96) * mm, "end": v(-38.27, 89.96) * mm});
            skLineSegment(sketch, "E46.left", {"start": v(-63.67, 96.31) * mm, "end": v(-63.67, 89.96) * mm});
            skLineSegment(sketch, "E46.right", {"start": v(-38.27, 96.31) * mm, "end": v(-38.27, 89.96) * mm});
            skLineSegment(sketch, "E47.bottom", {"start": v(-12.87, 96.31) * mm, "end": v(-0.17, 96.31) * mm});
            skLineSegment(sketch, "E47.top", {"start": v(-12.87, 89.96) * mm, "end": v(-0.17, 89.96) * mm});
            skLineSegment(sketch, "E47.left", {"start": v(-12.87, 96.31) * mm, "end": v(-12.87, 89.96) * mm});
            skLineSegment(sketch, "E47.right", {"start": v(-0.17, 96.31) * mm, "end": v(-0.17, 89.96) * mm});
            skLineSegment(sketch, "E48.bottom", {"start": v(-0.17, 210.61) * mm, "end": v(6.18, 210.61) * mm});
            skLineSegment(sketch, "E48.top", {"start": v(-0.17, 185.21) * mm, "end": v(6.18, 185.21) * mm});
            skLineSegment(sketch, "E48.left", {"start": v(-0.17, 210.61) * mm, "end": v(-0.17, 185.21) * mm});
            skLineSegment(sketch, "E48.right", {"start": v(6.18, 210.61) * mm, "end": v(6.18, 185.21) * mm});
            skLineSegment(sketch, "E49.bottom", {"start": v(-0.17, 147.11) * mm, "end": v(6.18, 147.11) * mm});
            skLineSegment(sketch, "E49.top", {"start": v(-0.17, 121.71) * mm, "end": v(6.18, 121.71) * mm});
            skLineSegment(sketch, "E49.left", {"start": v(-0.17, 147.11) * mm, "end": v(-0.17, 121.71) * mm});
            skLineSegment(sketch, "E49.right", {"start": v(6.18, 147.11) * mm, "end": v(6.18, 121.71) * mm});
            skLineSegment(sketch, "E50.bottom", {"start": v(-304.97, 210.61) * mm, "end": v(-298.62, 210.61) * mm});
            skLineSegment(sketch, "E50.top", {"start": v(-304.97, 185.21) * mm, "end": v(-298.62, 185.21) * mm});
            skLineSegment(sketch, "E50.right", {"start": v(-298.62, 210.61) * mm, "end": v(-298.62, 185.21) * mm});
            skLineSegment(sketch, "E51.bottom", {"start": v(-304.97, 147.11) * mm, "end": v(-298.62, 147.11) * mm});
            skLineSegment(sketch, "E51.top", {"start": v(-304.97, 121.71) * mm, "end": v(-298.62, 121.71) * mm});
            skLineSegment(sketch, "E51.right", {"start": v(-298.62, 147.11) * mm, "end": v(-298.62, 121.71) * mm});
            skLineSegment(sketch, "E52.trimOffspring", {"start": v(-304.97, 185.21) * mm, "end": v(-304.97, 147.11) * mm});
            skLineSegment(sketch, "E53.trimOffspring", {"start": v(-304.97, 121.71) * mm, "end": v(-304.97, 96.31) * mm});
            skSolve(sketch);
        }
        {
            var Q0;
            Q0 = qSketchRegion(id + "F6", true);
            extrude(context, id + "F7", {"entities" : qUnion([Q0]), "oppositeDirection" : true, "depth" : 6.35 * mm, "offsetDistance" : 25.4 * mm});
        }
        {
            var Q0;
            Q0=makeQuery(id+"F3.opExtrude","CAP_FACE",FACE,{"disambiguationData":[OSD([sQuery(id+"F2.wireOp",EDGE,"E11.bottom"),sQuery(id+"F2.wireOp",EDGE,"E11.top"),sQuery(id+"F2.wireOp",EDGE,"E11.left"),sQuery(id+"F2.wireOp",EDGE,"E11.right"),sQuery(id+"F2.wireOp",EDGE,"E12.bottom"),sQuery(id+"F2.wireOp",EDGE,"E12.top"),sQuery(id+"F2.wireOp",EDGE,"E12.right"),sQuery(id+"F2.wireOp",EDGE,"E13.bottom"),sQuery(id+"F2.wireOp",EDGE,"E13.top"),sQuery(id+"F2.wireOp",EDGE,"E13.right"),sQuery(id+"F2.wireOp",EDGE,"E14.trimOffspring"),sQuery(id+"F2.wireOp",EDGE,"E15.trimOffspring"),sQuery(id+"F2.wireOp",EDGE,"E16.top"),sQuery(id+"F2.wireOp",EDGE,"E16.left"),sQuery(id+"F2.wireOp",EDGE,"E16.right"),sQuery(id+"F2.wireOp",EDGE,"E17.1.0.1"),sQuery(id+"F2.wireOp",EDGE,"E17.1.0.2"),sQuery(id+"F2.wireOp",EDGE,"E17.1.0.3"),sQuery(id+"F2.wireOp",EDGE,"E17.2.0.1"),sQuery(id+"F2.wireOp",EDGE,"E17.2.0.2"),sQuery(id+"F2.wireOp",EDGE,"E17.2.0.3"),sQuery(id+"F2.wireOp",EDGE,"E17.3.0.1"),sQuery(id+"F2.wireOp",EDGE,"E17.3.0.2"),sQuery(id+"F2.wireOp",EDGE,"E17.3.0.3"),sQuery(id+"F2.wireOp",EDGE,"E17.4.0.1"),sQuery(id+"F2.wireOp",EDGE,"E17.4.0.2"),sQuery(id+"F2.wireOp",EDGE,"E17.4.0.3"),sQuery(id+"F2.wireOp",EDGE,"E17.5.0.1"),sQuery(id+"F2.wireOp",EDGE,"E17.5.0.2"),sQuery(id+"F2.wireOp",EDGE,"E17.5.0.3"),sQuery(id+"F2.wireOp",EDGE,"E18.top"),sQuery(id+"F2.wireOp",EDGE,"E18.left"),sQuery(id+"F2.wireOp",EDGE,"E18.right"),sQuery(id+"F2.wireOp",EDGE,"E19.1.0.0"),sQuery(id+"F2.wireOp",EDGE,"E19.1.0.2"),sQuery(id+"F2.wireOp",EDGE,"E19.1.0.3"),sQuery(id+"F2.wireOp",EDGE,"E19.2.0.0"),sQuery(id+"F2.wireOp",EDGE,"E19.2.0.2"),sQuery(id+"F2.wireOp",EDGE,"E19.2.0.3"),sQuery(id+"F2.wireOp",EDGE,"E19.3.0.0"),sQuery(id+"F2.wireOp",EDGE,"E19.3.0.2"),sQuery(id+"F2.wireOp",EDGE,"E19.3.0.3"),sQuery(id+"F2.wireOp",EDGE,"E19.4.0.0"),sQuery(id+"F2.wireOp",EDGE,"E19.4.0.2"),sQuery(id+"F2.wireOp",EDGE,"E19.4.0.3"),sQuery(id+"F2.wireOp",EDGE,"E19.5.0.0"),sQuery(id+"F2.wireOp",EDGE,"E19.5.0.2"),sQuery(id+"F2.wireOp",EDGE,"E19.5.0.3"),sQuery(id+"F2.wireOp",EDGE,"E20.bottom"),sQuery(id+"F2.wireOp",EDGE,"E20.top"),sQuery(id+"F2.wireOp",EDGE,"E20.right"),sQuery(id+"F2.wireOp",EDGE,"E21.bottom"),sQuery(id+"F2.wireOp",EDGE,"E21.top"),sQuery(id+"F2.wireOp",EDGE,"E21.right"),sQuery(id+"F2.wireOp",EDGE,"E22")])],"isStart":true});
            var sketch = newSketch(context, id + "F8", { "sketchPlane" : qUnion([Q0])});
            skLineSegment(sketch, "E54.bottom", {"start": v(596.73, 89.96) * mm, "end": v(736.43, 89.96) * mm});
            skLineSegment(sketch, "E54.top", {"start": v(596.73, -62.44) * mm, "end": v(736.43, -62.44) * mm});
            skLineSegment(sketch, "E54.left", {"start": v(596.73, 89.96) * mm, "end": v(596.73, -62.44) * mm});
            skLineSegment(sketch, "E54.right", {"start": v(736.43, 89.96) * mm, "end": v(736.43, 39.16) * mm});
            skLineSegment(sketch, "E55.bottom", {"start": v(596.73, 45.51) * mm, "end": v(590.38, 45.51) * mm});
            skLineSegment(sketch, "E55.top", {"start": v(596.73, 70.91) * mm, "end": v(590.38, 70.91) * mm});
            skLineSegment(sketch, "E55.left", {"start": v(596.73, 45.51) * mm, "end": v(596.73, 70.91) * mm});
            skLineSegment(sketch, "E55.right", {"start": v(590.38, 45.51) * mm, "end": v(590.38, 70.91) * mm});
            skLineSegment(sketch, "E56.bottom", {"start": v(596.73, -43.39) * mm, "end": v(590.38, -43.39) * mm});
            skLineSegment(sketch, "E56.top", {"start": v(596.73, -17.99) * mm, "end": v(590.38, -17.99) * mm});
            skLineSegment(sketch, "E56.left", {"start": v(596.73, -43.39) * mm, "end": v(596.73, -17.99) * mm});
            skLineSegment(sketch, "E56.right", {"start": v(590.38, -43.39) * mm, "end": v(590.38, -17.99) * mm});
            skLineSegment(sketch, "E57.bottom", {"start": v(622.13, 89.96) * mm, "end": v(647.53, 89.96) * mm});
            skLineSegment(sketch, "E57.top", {"start": v(622.13, 96.31) * mm, "end": v(647.53, 96.31) * mm});
            skLineSegment(sketch, "E57.left", {"start": v(622.13, 96.31) * mm, "end": v(622.13, 89.96) * mm});
            skLineSegment(sketch, "E57.right", {"start": v(647.53, 96.31) * mm, "end": v(647.53, 89.96) * mm});
            skLineSegment(sketch, "E58.bottom", {"start": v(685.63, 89.96) * mm, "end": v(711.03, 89.96) * mm});
            skLineSegment(sketch, "E58.top", {"start": v(685.63, 96.31) * mm, "end": v(711.03, 96.31) * mm});
            skLineSegment(sketch, "E58.left", {"start": v(685.63, 96.31) * mm, "end": v(685.63, 89.96) * mm});
            skLineSegment(sketch, "E58.right", {"start": v(711.03, 96.31) * mm, "end": v(711.03, 89.96) * mm});
            skLineSegment(sketch, "E59.bottom", {"start": v(622.13, -62.44) * mm, "end": v(647.53, -62.44) * mm});
            skLineSegment(sketch, "E59.top", {"start": v(622.13, -68.79) * mm, "end": v(647.53, -68.79) * mm});
            skLineSegment(sketch, "E59.left", {"start": v(622.13, -62.44) * mm, "end": v(622.13, -68.79) * mm});
            skLineSegment(sketch, "E59.right", {"start": v(647.53, -62.44) * mm, "end": v(647.53, -68.79) * mm});
            skLineSegment(sketch, "E60.bottom", {"start": v(685.63, -62.44) * mm, "end": v(711.03, -62.44) * mm});
            skLineSegment(sketch, "E60.top", {"start": v(685.63, -68.79) * mm, "end": v(711.03, -68.79) * mm});
            skLineSegment(sketch, "E60.left", {"start": v(685.63, -62.44) * mm, "end": v(685.63, -68.79) * mm});
            skLineSegment(sketch, "E60.right", {"start": v(711.03, -62.44) * mm, "end": v(711.03, -68.79) * mm});
            skArc(sketch, "E61", {"start": v(736.43, 39.16) * mm, "mid": v(711.03, 13.76) * mm, "end": v(736.43, -11.64) * mm});
            skLineSegment(sketch, "E62.trimOffspring", {"start": v(736.43, -11.64) * mm, "end": v(736.43, -62.44) * mm});
            skSolve(sketch);
        }
        {
            var Q0;
            Q0 = qSketchRegion(id + "F8", true);
            extrude(context, id + "F9", {"entities" : qUnion([Q0]), "oppositeDirection" : true, "depth" : 6.35 * mm, "offsetDistance" : 25.4 * mm});
        }
    });
